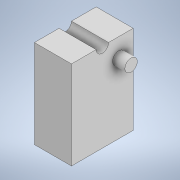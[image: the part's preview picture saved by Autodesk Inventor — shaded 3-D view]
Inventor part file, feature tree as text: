
AUTODESK INVENTOR PART (.ipt)
format: ipt  version: 2021 (Build 250183000, 183)  size: 139,776 bytes
history: native  units: mm
features: sketch x4, extrude x3, emboss x1
ambient origin geometry x8: Origin, YZ Plane, XZ Plane, XY Plane, X Axis, Y Axis, Z Axis, Center Point
bodies: Solid1 (feature_tree)
feature tree (8):
  extrude  "Extrusion1"  Depth=15.0mm
  extrude  "Extrusion2"  Depth=7.5mm
  extrude  "Extrusion3"  Depth=3.0mm
  emboss  "Emboss1"
  sketch  "Sketch1"  dims[d0=21.477mm d1=15.0mm]
  sketch  "Sketch2"  dims[d2=10.7385mm d3=7.5mm]
  sketch  "Sketch3"  dims[d4=9.0mm d5=0.0mm d8=3.0mm]
  sketch  "Sketch4"  dims[d10=0.0mm d11=0.0mm d12=3.0mm d13=3.983mm d14=4.478mm d15=3.0mm d16=0.0mm d17=1.0mm d18=0.0mm]
